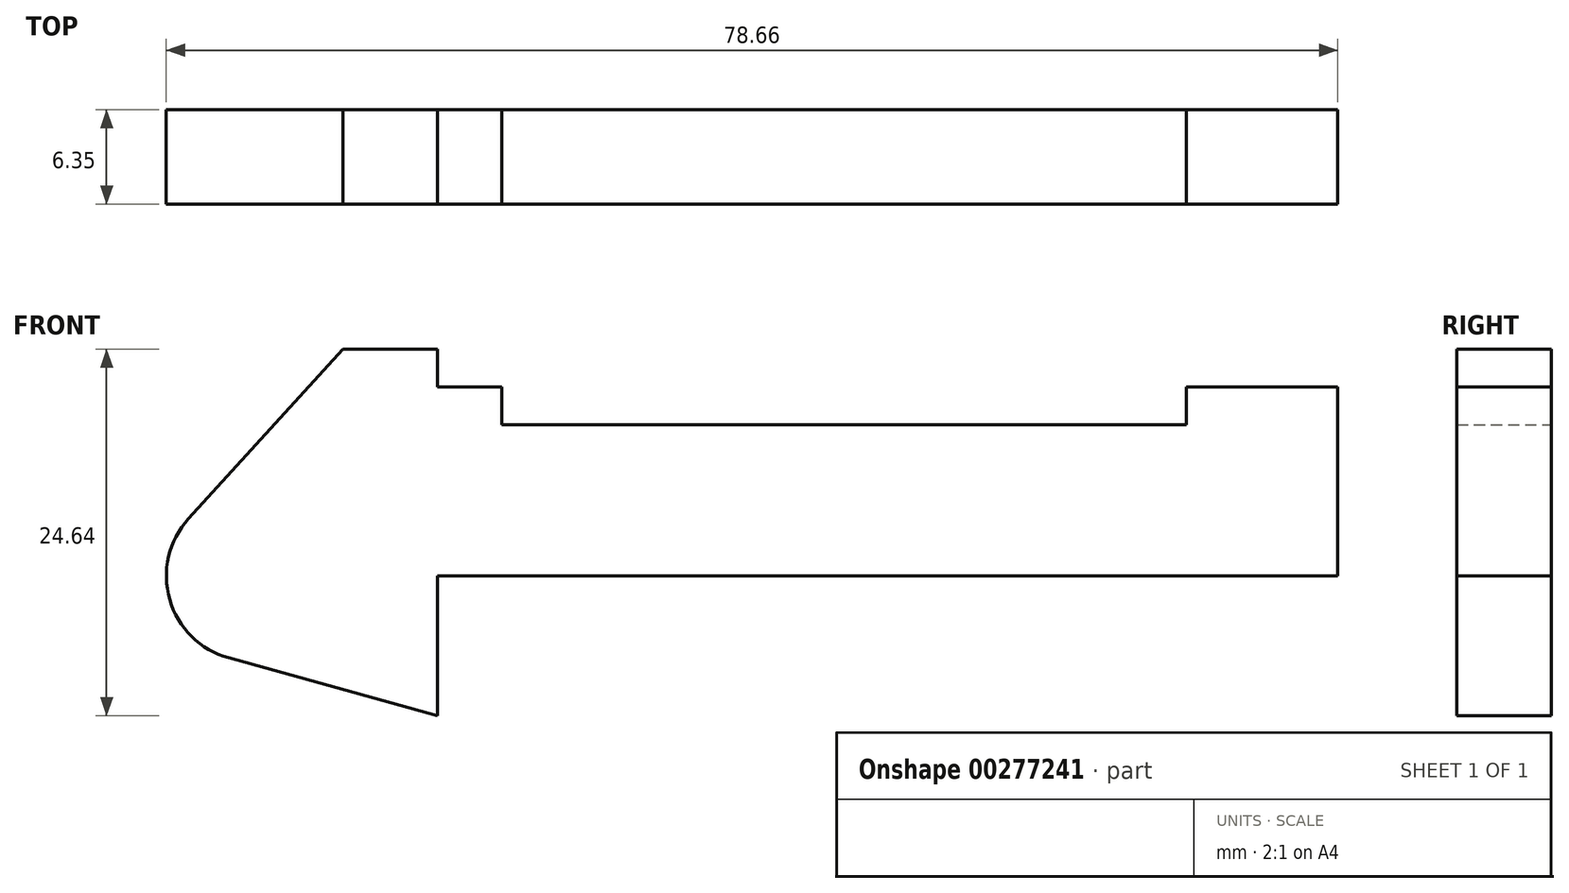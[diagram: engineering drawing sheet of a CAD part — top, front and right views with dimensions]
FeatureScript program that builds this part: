
annotation { "Feature Type Name" : "Feature", "Feature Type Description" : "" }
export const myFeature = defineFeature(function(context is Context, id is Id, definition is map)
    precondition{}
    {
        {
            var Q0;
            Q0=qCreatedBy(makeId("Front.planeOp"),FACE);
            var sketch = newSketch(context, id + "F0", { "sketchPlane" : qUnion([Q0])});
            skLineSegment(sketch, "E0", {"start": v(0, 0) * mm, "end": v(0, 12.7) * mm});
            skLineSegment(sketch, "E1", {"start": v(0, 12.7) * mm, "end": v(10.16, 12.7) * mm});
            skLineSegment(sketch, "E2", {"start": v(10.16, 12.7) * mm, "end": v(10.16, 10.16) * mm});
            skLineSegment(sketch, "E3", {"start": v(10.16, 10.16) * mm, "end": v(56.13, 10.16) * mm});
            skLineSegment(sketch, "E4", {"start": v(56.13, 10.16) * mm, "end": v(56.13, 12.7) * mm});
            skLineSegment(sketch, "E5", {"start": v(56.13, 12.7) * mm, "end": v(66.3, 12.7) * mm});
            skLineSegment(sketch, "E6", {"start": v(66.3, 12.7) * mm, "end": v(66.3, 0) * mm});
            skLineSegment(sketch, "E7", {"start": v(66.3, 0) * mm, "end": v(0, 0) * mm});
            skLineSegment(sketch, "E8", {"start": v(5.84, 15.24) * mm, "end": v(-0.5, 15.24) * mm});
            skLineSegment(sketch, "E9", {"start": v(-0.5, 15.24) * mm, "end": v(-10.88, 3.85) * mm});
            skLineSegment(sketch, "E10", {"start": v(0, 0) * mm, "end": v(-6.65, 0) * mm});
            skCircle(sketch, "E11", {"center": v(-6.65, 0) * mm, "radius": 5.72 * mm});
            skCircle(sketch, "E12", {"center": v(-6.65, 0) * mm, "radius": 3.18 * mm});
            skLineSegment(sketch, "E13", {"start": v(5.84, 15.24) * mm, "end": v(5.84, -9.4) * mm});
            skLineSegment(sketch, "E14", {"start": v(5.84, -9.4) * mm, "end": v(-8.18, -5.5) * mm});
            skSolve(sketch);
        }
        {
            var Q0;
            {var subQ0=sQuery(id+"F0.wireOp",EDGE,"E2");Q0=makeQuery(id+"F0.imprint","IMPRINT",FACE,{"disambiguationData":[TD([[makeQuery(id+"F0.imprint","IMPRINT",EDGE,{"derivedFrom":subQ0}),-1.0]])]});}
            var Q1;
            {var subQ0=sQuery(id+"F0.wireOp",EDGE,"E12");Q1=makeQuery(id+"F0.imprint","IMPRINT",FACE,{"disambiguationData":[TD([[makeQuery(id+"F0.imprint","IMPRINT",EDGE,{"derivedFrom":subQ0}),1.0]])]});}
            var Q2;
            {var subQ0=sQuery(id+"F0.wireOp",EDGE,"E0");Q2=makeQuery(id+"F0.imprint","IMPRINT",FACE,{"disambiguationData":[TD([[makeQuery(id+"F0.imprint","IMPRINT",EDGE,{"derivedFrom":subQ0}),-1.0]])]});}
            var Q3;
            {var subQ3=sQuery(id+"F0.wireOp",EDGE,"E0");Q3=makeQuery(id+"F0.imprint","IMPRINT",FACE,{"disambiguationData":[TD([[makeQuery(id+"F0.imprint","IMPRINT",EDGE,{"derivedFrom":subQ3}),1.0]])]});}
            var Q4;
            {var subQ0=sQuery(id+"F0.wireOp",EDGE,"E14");Q4=makeQuery(id+"F0.imprint","IMPRINT",FACE,{"disambiguationData":[TD([[makeQuery(id+"F0.imprint","IMPRINT",EDGE,{"derivedFrom":subQ0}),-1.0]])]});}
            var Q5;
            {var subQ4=sQuery(id+"F0.wireOp",EDGE,"E12");Q5=makeQuery(id+"F0.imprint","IMPRINT",FACE,{"disambiguationData":[TD([[makeQuery(id+"F0.imprint","IMPRINT",EDGE,{"derivedFrom":subQ4}),-1.0]])]});}
            extrude(context, id + "F1", {"entities" : qUnion([Q0, Q1, Q2, Q3, Q4, Q5]), "depth" : 6.35 * mm});
        }
    });
